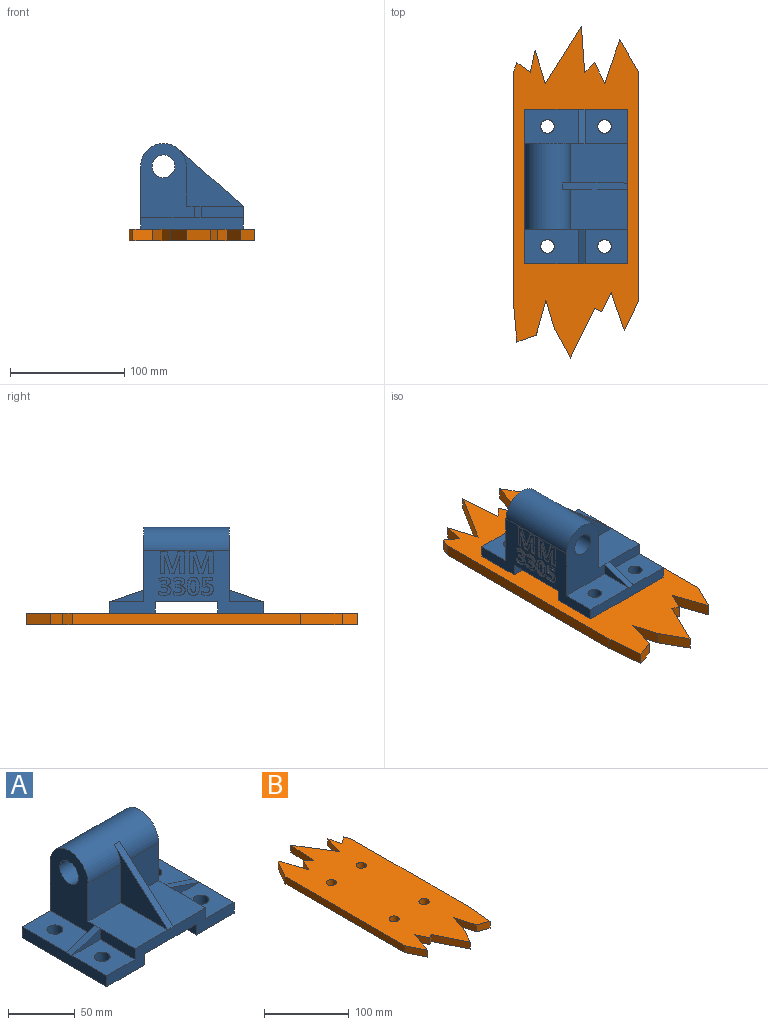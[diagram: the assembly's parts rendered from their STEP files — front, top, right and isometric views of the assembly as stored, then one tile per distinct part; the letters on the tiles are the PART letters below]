
ASSEMBLY  parts=2 mates=1
PART A: 171 faces, bbox 135x90x75 mm
  f0: plane 135x55mm, normal (0,1,0), area 3247.7mm2, adj f3,f4,f8,f9,f10,f11,f14,f21
  f1: plane 50x34.5mm, normal (0,0,1), area 1725mm2, adj f2,f3,f6,f12,f18,f34
  f2: plane 35x34.5mm, normal (0,-1,0), area 1207.5mm2, adj f1,f3,f14,f34
  f3: plane 65x47mm, normal (-1,0,0), area 2184.2mm2, adj f0,f1,f2,f4,f14,f15,f17
  f4: plane 47x30mm, normal (0,0,1), area 1296.9mm2, adj f0,f3,f8,f17,f19
  f5: plane 50x34.5mm, normal (0,0,1), area 1725mm2, adj f12,f13,f21,f23,f30,f33
  f6: plane 37x10mm, normal (-1,0,0), area 370mm2, adj f1,f7,f12,f16
  f7: plane 37x30mm, normal (0,0,1), area 996.9mm2, adj f6,f8,f12,f16,f20
  f8: plane 90x10mm, normal (-1,0,0), area 900mm2, adj f0,f4,f7,f9,f12,f18
  f9: plane 90x40mm, normal (0,0,-1), area 3373.8mm2, adj f0,f8,f10,f12,f19,f20
  f10: plane 90x10mm, normal (1,0,0), area 900mm2, adj f0,f9,f11,f12
  f11: plane 90x55mm, normal (0,0,-1), area 4950mm2, adj f0,f10,f12,f27
  f12: plane 135x20mm, normal (0,-1,0), area 1550mm2, adj f1,f5,f6,f7,f8,f9,f10,f11
  f13: plane 35x34.5mm, normal (0,-1,0), area 1207.5mm2, adj f5,f14,f21,f33
  f14: cylinder r=20mm len=75mm, axis (-1,0,0), area 4610.5mm2, adj f0,f2,f3,f13,f21,f33,f34,f35
  f15: cylinder r=10mm len=75mm, axis (-1,0,0), area 4712.4mm2, adj f3,f21
  f16: plane 30x10mm, normal (0,-1,0), area 150mm2, adj f6,f7,f18
  f17: plane 30x10mm, normal (0,1,0), area 150mm2, adj f3,f4,f18
  f18: plane 30x10mm, normal (-0.32,0,0.95), area 189.7mm2, adj f1,f8,f16,f17
  f19: cylinder r=6mm len=12mm, axis (0,0,1), area 377mm2, adj f4,f9
  f20: cylinder r=6mm len=12mm, axis (0,0,1), area 377mm2, adj f7,f9
  f21: plane 65x47mm, normal (1,0,0), area 2184.2mm2, adj f0,f5,f13,f14,f15,f22,f29
  f22: plane 47x30mm, normal (0,0,1), area 1296.9mm2, adj f0,f21,f25,f29,f31
  f23: plane 37x10mm, normal (1,0,0), area 370mm2, adj f5,f12,f24,f28
  f24: plane 37x30mm, normal (0,0,1), area 996.9mm2, adj f12,f23,f25,f28,f32
  f25: plane 90x10mm, normal (1,0,0), area 900mm2, adj f0,f12,f22,f24,f26,f30
  f26: plane 90x40mm, normal (0,0,-1), area 3373.8mm2, adj f0,f12,f25,f27,f31,f32
  f27: plane 90x10mm, normal (-1,0,0), area 900mm2, adj f0,f11,f12,f26
  f28: plane 30x10mm, normal (0,-1,0), area 150mm2, adj f23,f24,f30
  f29: plane 30x10mm, normal (0,1,0), area 150mm2, adj f21,f22,f30
  f30: plane 30x10mm, normal (0.32,0,0.95), area 189.7mm2, adj f5,f25,f28,f29
  f31: cylinder r=6mm len=12mm, axis (0,0,1), area 377mm2, adj f22,f26
  f32: cylinder r=6mm len=12mm, axis (0,0,1), area 377mm2, adj f24,f26
  f33: plane 56.78x50.01mm, normal (1,0,0), area 1111.9mm2, adj f5,f13,f14,f35
  f34: plane 56.78x50.01mm, normal (-1,0,0), area 1111.9mm2, adj f1,f2,f14,f35
  f35: plane 56.78x50.01mm, normal (0,-0.66,0.75), area 454mm2, adj f12,f14,f33,f34
  f36: plane 3.73x1mm, normal (0,0,1), area 3.7mm2, adj f0,f37,f54,f55
  f37: plane 15.02x4.95mm, normal (0.95,0,0.31), area 15.8mm2, adj f0,f36,f38,f55
  f38: plane 1x0.12mm, normal (0,0,1), area 0.1mm2, adj f0,f37,f39,f55
  f39: extruded ~4.46x1mm, area 4.5mm2, adj f0,f38,f40,f55
  f40: extruded ~1.48x1mm, area 1.5mm2, adj f0,f39,f41,f55
  f41: plane 9.08x1mm, normal (-1,0,0), area 9.1mm2, adj f0,f40,f42,f55
  f42: plane 3.79x1mm, normal (0,0,1), area 3.8mm2, adj f0,f41,f43,f55
  f43: plane 19.18x1mm, normal (1,0,0), area 19.2mm2, adj f0,f42,f44,f55
  f44: plane 5.53x1mm, normal (0,0,-1), area 5.5mm2, adj f0,f43,f45,f55
  f45: plane 14.67x4.82mm, normal (-0.95,0,-0.31), area 15.4mm2, adj f0,f44,f46,f55
  f46: plane 1x0.08mm, normal (0,0,-1), area 0.1mm2, adj f0,f45,f47,f55
  f47: plane 14.67x4.54mm, normal (0.96,0,-0.3), area 15.4mm2, adj f0,f46,f48,f55
  f48: plane 5.54x1mm, normal (0,0,-1), area 5.5mm2, adj f0,f47,f49,f55
  f49: plane 19.18x1mm, normal (-1,0,0), area 19.2mm2, adj f0,f48,f50,f55
  f50: plane 3.64x1mm, normal (0,0,1), area 3.6mm2, adj f0,f49,f51,f55
  f51: plane 8.92x1mm, normal (1,0,0), area 8.9mm2, adj f0,f50,f52,f55
  f52: extruded ~6.13x1mm, area 6.1mm2, adj f0,f51,f53,f55
  f53: plane 1x0.12mm, normal (0,0,1), area 0.1mm2, adj f0,f52,f54,f55
  f54: plane 15.05x4.62mm, normal (-0.96,0,0.29), area 15.7mm2, adj f0,f36,f53,f55
  f55: plane 20.51x19.18mm, normal (0,1,0), area 253.8mm2, adj f36,f37,f38,f39,f40,f41,f42,f43
  f56: extruded ~5.95x1.37mm, area 6.2mm2, adj f0,f57,f71,f72
  f57: extruded ~4.05x2.03mm, area 4.7mm2, adj f0,f56,f58,f72
  f58: extruded ~4.08x1.94mm, area 4.7mm2, adj f0,f57,f59,f72
  f59: extruded ~6.04x1.32mm, area 6.3mm2, adj f0,f58,f60,f72
  f60: extruded ~5.94x1.36mm, area 6.2mm2, adj f0,f59,f61,f72
  f61: extruded ~4.04x2.01mm, area 4.7mm2, adj f0,f60,f62,f72
  f62: extruded ~4.09x1.95mm, area 4.7mm2, adj f0,f61,f71,f72
  f63: extruded ~4.09x1mm, area 4.1mm2, adj f64,f70,f72,f73
  f64: extruded ~1.65x1.24mm, area 2.2mm2, adj f63,f65,f72,f73
  f65: extruded ~1.65x1.24mm, area 2.2mm2, adj f64,f66,f72,f73
  f66: extruded ~4.09x1mm, area 4.1mm2, adj f65,f67,f72,f73
  f67: extruded ~4.06x1mm, area 4.1mm2, adj f66,f68,f72,f73
  f68: extruded ~1.65x1.25mm, area 2.2mm2, adj f67,f69,f72,f73
  f69: extruded ~1.66x1.23mm, area 2.2mm2, adj f68,f70,f72,f73
  f70: extruded ~4.08x1mm, area 4.1mm2, adj f63,f69,f72,f73
  f71: extruded ~6x1.33mm, area 6.2mm2, adj f0,f56,f62,f72
  f72: plane 15.94x10.82mm, normal (0,1,0), area 104.9mm2, adj f56,f57,f58,f59,f60,f61,f62,f63
  f73: plane 10.65x4.31mm, normal (0,1,0), area 39mm2, adj f63,f64,f65,f66,f67,f68,f69,f70
  f74: plane 3.73x1mm, normal (0,0,1), area 3.7mm2, adj f0,f75,f92,f93
  f75: plane 15.02x4.95mm, normal (0.95,0,0.31), area 15.8mm2, adj f0,f74,f76,f93
  f76: plane 1x0.12mm, normal (0,0,1), area 0.1mm2, adj f0,f75,f77,f93
  f77: extruded ~4.46x1mm, area 4.5mm2, adj f0,f76,f78,f93
  f78: extruded ~1.48x1mm, area 1.5mm2, adj f0,f77,f79,f93
  f79: plane 9.08x1mm, normal (-1,0,0), area 9.1mm2, adj f0,f78,f80,f93
  f80: plane 3.79x1mm, normal (0,0,1), area 3.8mm2, adj f0,f79,f81,f93
  f81: plane 19.18x1mm, normal (1,0,0), area 19.2mm2, adj f0,f80,f82,f93
  f82: plane 5.53x1mm, normal (0,0,-1), area 5.5mm2, adj f0,f81,f83,f93
  f83: plane 14.67x4.82mm, normal (-0.95,0,-0.31), area 15.4mm2, adj f0,f82,f84,f93
  f84: plane 1x0.08mm, normal (0,0,-1), area 0.1mm2, adj f0,f83,f85,f93
  f85: plane 14.67x4.54mm, normal (0.96,0,-0.3), area 15.4mm2, adj f0,f84,f86,f93
  f86: plane 5.54x1mm, normal (0,0,-1), area 5.5mm2, adj f0,f85,f87,f93
  f87: plane 19.18x1mm, normal (-1,0,0), area 19.2mm2, adj f0,f86,f88,f93
  f88: plane 3.64x1mm, normal (0,0,1), area 3.6mm2, adj f0,f87,f89,f93
  f89: plane 8.92x1mm, normal (1,0,0), area 8.9mm2, adj f0,f88,f90,f93
  f90: extruded ~6.13x1mm, area 6.1mm2, adj f0,f89,f91,f93
  f91: plane 1x0.12mm, normal (0,0,1), area 0.1mm2, adj f0,f90,f92,f93
  f92: plane 15.05x4.62mm, normal (-0.96,0,0.29), area 15.7mm2, adj f0,f74,f91,f93
  f93: plane 20.51x19.18mm, normal (0,1,0), area 253.8mm2, adj f74,f75,f76,f77,f78,f79,f80,f81
  f94: extruded ~2.71x1.39mm, area 3.2mm2, adj f0,f95,f120,f121
  f95: extruded ~3.79x1mm, area 4mm2, adj f0,f94,f96,f121
  f96: extruded ~5.05x1.52mm, area 5.4mm2, adj f0,f95,f97,f121
  f97: plane 2.25x1.51mm, normal (-0.83,0,0.56), area 2.7mm2, adj f0,f96,f98,f121
  f98: extruded ~1.75x1mm, area 2mm2, adj f0,f97,f99,f121
  f99: extruded ~1.55x1mm, area 1.6mm2, adj f0,f98,f100,f121
  f100: extruded ~2.2x1.76mm, area 3.2mm2, adj f0,f99,f101,f121
  f101: extruded ~1.61x1mm, area 1.9mm2, adj f0,f100,f102,f121
  f102: extruded ~2.63x1mm, area 2.7mm2, adj f0,f101,f103,f121
  f103: plane 1.2x1mm, normal (0,0,-1), area 1.2mm2, adj f0,f102,f104,f121
  f104: plane 2.51x1mm, normal (-1,0,0), area 2.5mm2, adj f0,f103,f105,f121
  f105: plane 1.18x1mm, normal (0,0,1), area 1.2mm2, adj f0,f104,f106,f121
  f106: extruded ~2.84x1mm, area 2.9mm2, adj f0,f105,f107,f121
  f107: extruded ~1.54x1mm, area 1.9mm2, adj f0,f106,f108,f121
  f108: extruded ~1.77x1mm, area 2mm2, adj f0,f107,f109,f121
  f109: extruded ~2.4x1mm, area 2.5mm2, adj f0,f108,f110,f121
  f110: extruded ~2.14x1mm, area 2.2mm2, adj f0,f109,f111,f121
  f111: extruded ~1.98x1mm, area 2.1mm2, adj f0,f110,f112,f121
  f112: plane 2.79x1mm, normal (-1,0,0), area 2.8mm2, adj f0,f111,f113,f121
  f113: extruded ~4.47x1mm, area 4.6mm2, adj f0,f112,f114,f121
  f114: extruded ~4.62x1.25mm, area 4.9mm2, adj f0,f113,f115,f121
  f115: extruded ~3.48x1.62mm, area 4mm2, adj f0,f114,f116,f121
  f116: extruded ~2.44x1mm, area 2.7mm2, adj f0,f115,f117,f121
  f117: extruded ~2.84x1.14mm, area 3.1mm2, adj f0,f116,f118,f121
  f118: plane 1x0.06mm, normal (1,0,0), area 0.1mm2, adj f0,f117,f119,f121
  f119: extruded ~2.47x1.4mm, area 2.9mm2, adj f0,f118,f120,f121
  f120: extruded ~2.47x1mm, area 2.7mm2, adj f0,f94,f119,f121
  f121: plane 15.91x10.71mm, normal (0,1,0), area 90.6mm2, adj f94,f95,f96,f97,f98,f99,f100,f101
  f122: extruded ~2.71x1.39mm, area 3.2mm2, adj f0,f123,f148,f149
  f123: extruded ~3.79x1mm, area 4mm2, adj f0,f122,f124,f149
  f124: extruded ~5.05x1.52mm, area 5.4mm2, adj f0,f123,f125,f149
  f125: plane 2.25x1.51mm, normal (-0.83,0,0.56), area 2.7mm2, adj f0,f124,f126,f149
  f126: extruded ~1.75x1mm, area 2mm2, adj f0,f125,f127,f149
  f127: extruded ~1.55x1mm, area 1.6mm2, adj f0,f126,f128,f149
  f128: extruded ~2.2x1.76mm, area 3.2mm2, adj f0,f127,f129,f149
  f129: extruded ~1.61x1mm, area 1.9mm2, adj f0,f128,f130,f149
  f130: extruded ~2.63x1mm, area 2.7mm2, adj f0,f129,f131,f149
  f131: plane 1.2x1mm, normal (0,0,-1), area 1.2mm2, adj f0,f130,f132,f149
  f132: plane 2.51x1mm, normal (-1,0,0), area 2.5mm2, adj f0,f131,f133,f149
  f133: plane 1.18x1mm, normal (0,0,1), area 1.2mm2, adj f0,f132,f134,f149
  f134: extruded ~2.84x1mm, area 2.9mm2, adj f0,f133,f135,f149
  f135: extruded ~1.54x1mm, area 1.9mm2, adj f0,f134,f136,f149
  f136: extruded ~1.77x1mm, area 2mm2, adj f0,f135,f137,f149
  f137: extruded ~2.4x1mm, area 2.5mm2, adj f0,f136,f138,f149
  f138: extruded ~2.14x1mm, area 2.2mm2, adj f0,f137,f139,f149
  f139: extruded ~1.98x1mm, area 2.1mm2, adj f0,f138,f140,f149
  f140: plane 2.79x1mm, normal (-1,0,0), area 2.8mm2, adj f0,f139,f141,f149
  f141: extruded ~4.47x1mm, area 4.6mm2, adj f0,f140,f142,f149
  f142: extruded ~4.62x1.25mm, area 4.9mm2, adj f0,f141,f143,f149
  f143: extruded ~3.48x1.62mm, area 4mm2, adj f0,f142,f144,f149
  f144: extruded ~2.44x1mm, area 2.7mm2, adj f0,f143,f145,f149
  f145: extruded ~2.84x1.14mm, area 3.1mm2, adj f0,f144,f146,f149
  f146: plane 1x0.06mm, normal (1,0,0), area 0.1mm2, adj f0,f145,f147,f149
  f147: extruded ~2.47x1.4mm, area 2.9mm2, adj f0,f146,f148,f149
  f148: extruded ~2.47x1mm, area 2.7mm2, adj f0,f122,f147,f149
  f149: plane 15.91x10.71mm, normal (0,1,0), area 90.6mm2, adj f122,f123,f124,f125,f126,f127,f128,f129
  f150: extruded ~1.6x1mm, area 1.6mm2, adj f0,f151,f169,f170
  f151: plane 1x0.37mm, normal (-0.2,0,-0.98), area 0.4mm2, adj f0,f150,f152,f170
  f152: plane 3.04x1mm, normal (1,0,0.09), area 3.1mm2, adj f0,f151,f153,f170
  f153: plane 5.53x1mm, normal (0,0,1), area 5.5mm2, adj f0,f152,f154,f170
  f154: plane 2.77x1mm, normal (1,0,0), area 2.8mm2, adj f0,f153,f155,f170
  f155: plane 8.4x1mm, normal (0,0,-1), area 8.4mm2, adj f0,f154,f156,f170
  f156: plane 7.89x1mm, normal (-1,0,-0.07), area 7.9mm2, adj f0,f155,f157,f170
  f157: plane 1.3x1mm, normal (-0.47,0,0.88), area 1.5mm2, adj f0,f156,f158,f170
  f158: extruded ~1.1x1mm, area 1.1mm2, adj f0,f157,f159,f170
  f159: extruded ~1.24x1mm, area 1.2mm2, adj f0,f158,f160,f170
  f160: extruded ~3.1x2.34mm, area 4.4mm2, adj f0,f159,f161,f170
  f161: extruded ~3x2.46mm, area 4.4mm2, adj f0,f160,f162,f170
  f162: extruded ~2.11x1mm, area 2.1mm2, adj f0,f161,f163,f170
  f163: extruded ~1.95x1mm, area 2.1mm2, adj f0,f162,f164,f170
  f164: plane 2.83x1mm, normal (-1,0,0), area 2.8mm2, adj f0,f163,f165,f170
  f165: extruded ~4.17x1mm, area 4.3mm2, adj f0,f164,f166,f170
  f166: extruded ~4.57x1.4mm, area 4.9mm2, adj f0,f165,f167,f170
  f167: extruded ~3.99x1.6mm, area 4.4mm2, adj f0,f166,f168,f170
  f168: extruded ~3.45x1.33mm, area 3.8mm2, adj f0,f167,f169,f170
  f169: extruded ~3.57x1.26mm, area 3.9mm2, adj f0,f150,f168,f170
  f170: plane 15.69x10.34mm, normal (0,1,0), area 94.6mm2, adj f150,f151,f152,f153,f154,f155,f156,f157
PART B: 28 faces, bbox 110x290.6x10 mm
  f0: plane 36.19x10mm, normal (1,-0.09,0), area 363.4mm2, adj f1,f21,f22,f23
  f1: plane 200x10mm, normal (1,0,0), area 2000mm2, adj f0,f2,f22,f23
  f2: plane 10x8.43mm, normal (0.93,0.37,0), area 90.6mm2, adj f1,f3,f22,f23
  f3: plane 11.59x10mm, normal (-0.59,0.81,0), area 143.3mm2, adj f2,f4,f22,f23
  f4: plane 18.94x10mm, normal (0.97,0.22,0), area 194.3mm2, adj f3,f5,f22,f23
  f5: plane 28.75x10mm, normal (-0.96,0.29,0), area 300.7mm2, adj f4,f6,f22,f23
  f6: plane 50.28x31.67mm, normal (0.85,0.53,0), area 594.2mm2, adj f5,f7,f22,f23
  f7: plane 40.47x10mm, normal (-1,0.07,0), area 405.7mm2, adj f6,f8,f22,f23
  f8: plane 10x8.71mm, normal (0.7,0.72,0), area 121.2mm2, adj f7,f9,f22,f23
  f9: plane 18.24x10mm, normal (-0.9,0.43,0), area 202.4mm2, adj f8,f10,f22,f23
  f10: plane 38.19x13.21mm, normal (0.95,0.33,0), area 404.1mm2, adj f9,f11,f22,f23
  f11: plane 28.38x16.69mm, normal (-0.86,0.51,0), area 329.2mm2, adj f10,f12,f22,f23
  f12: plane 200x10mm, normal (-1,0,0), area 2000mm2, adj f11,f13,f22,f23
  f13: plane 26.18x12.67mm, normal (-0.9,-0.44,0), area 290.8mm2, adj f12,f14,f22,f23
  f14: plane 33.68x11.65mm, normal (0.95,-0.33,0), area 356.4mm2, adj f13,f15,f22,f23
  f15: plane 16.94x10mm, normal (-0.9,-0.44,0), area 188.1mm2, adj f14,f16,f22,f23
  f16: plane 10x6.15mm, normal (0.44,-0.9,0), area 68.3mm2, adj f15,f17,f22,f23
  f17: plane 43.67x21.14mm, normal (-0.9,-0.44,0), area 485.1mm2, adj f16,f18,f22,f23
  f18: plane 25.59x14.14mm, normal (0.88,-0.48,0), area 292.4mm2, adj f17,f19,f22,f23
  f19: plane 24.54x10mm, normal (0.96,-0.29,0), area 256.2mm2, adj f18,f20,f22,f23
  f20: plane 30.02x10mm, normal (-0.96,-0.27,0), area 312mm2, adj f19,f21,f22,f23
  f21: plane 16.87x10mm, normal (-0.34,-0.94,0), area 179.6mm2, adj f0,f20,f22,f23
  f22: plane 290.6x110mm, normal (0,0,1), area 24919.5mm2, adj f0,f1,f2,f3,f4,f5,f6,f7
  f23: plane 290.6x110mm, normal (0,0,-1), area 24919.5mm2, adj f0,f1,f2,f3,f4,f5,f6,f7
  f24: cylinder r=6mm len=12mm, axis (0,0,1), area 377mm2, adj f22,f23
  f25: cylinder r=6mm len=12mm, axis (0,0,1), area 377mm2, adj f22,f23
  f26: cylinder r=6mm len=12mm, axis (0,0,1), area 377mm2, adj f22,f23
  f27: cylinder r=6mm len=12mm, axis (0,0,1), area 377mm2, adj f22,f23
PLACE A rot(axis=(0,0,1),90deg) t=(-49.74,-140.47,10)mm
PLACE B rot(axis=(0,1,0),180deg) t=(-4.74,-140.47,10)mm
MATE fastened A.f31 <-> B.f26  axis (0,0,-1) through (-29.74,-87.97,10)mm
